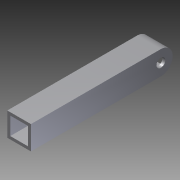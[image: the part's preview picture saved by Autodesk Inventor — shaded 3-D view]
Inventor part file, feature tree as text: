
AUTODESK INVENTOR PART (.ipt)
format: ipt  version: 2012 (Build 160160000, 160)  size: 97,280 bytes
history: native  units: in
note: dims shown in document units (in); Inventor stores cm internally (conversion verified against a paired STEP export)
features: extrude x2, sketch x2
ambient origin geometry x8: Origin, YZ Plane, XZ Plane, XY Plane, X Axis, Y Axis, Z Axis, Center Point
bodies: Solid1 (feature_tree)
feature tree (4):
  extrude  "Extrusion1"  Depth=1.0in
  extrude  "Extrusion2"  Depth=0.125in
  sketch  "Sketch1"  dims[d0=1.0in d1=1.0in]
  sketch  "Sketch2"  dims[d2=0.125in d3=0.125in d4=0.125in d5=0.125in d6=6.0in d7=0.0in d8=0.375in d9=0.5in d10=0.5in d11=1.0in d12=0.0in]
